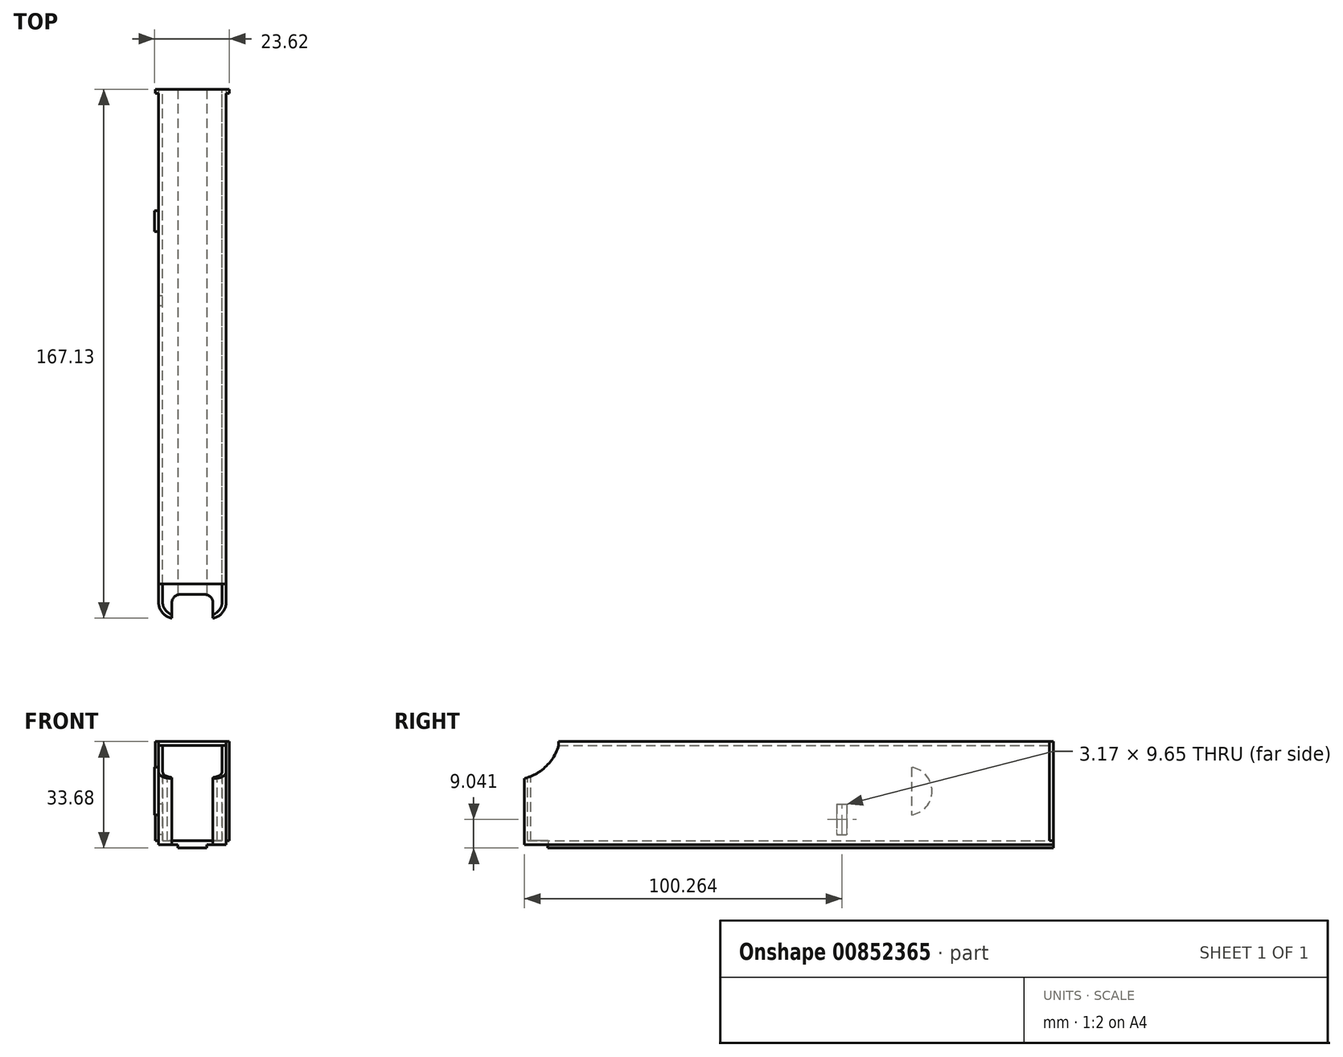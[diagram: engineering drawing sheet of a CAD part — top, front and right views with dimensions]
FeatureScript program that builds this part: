
annotation { "Feature Type Name" : "Feature", "Feature Type Description" : "" }
export const myFeature = defineFeature(function(context is Context, id is Id, definition is map)
    precondition{}
    {
        {
            var Q0;
            Q0=qCreatedBy(makeId("Front.planeOp"),FACE);
            var sketch = newSketch(context, id + "F0", { "sketchPlane" : qUnion([Q0])});
            skLineSegment(sketch, "E0.bottom", {"start": v(0, 0) * mm, "end": v(21.34, 0) * mm});
            skLineSegment(sketch, "E0.top", {"start": v(0, 32.64) * mm, "end": v(21.34, 32.64) * mm});
            skLineSegment(sketch, "E0.left", {"start": v(0, 0) * mm, "end": v(0, 32.64) * mm});
            skLineSegment(sketch, "E0.right", {"start": v(21.34, 0) * mm, "end": v(21.34, 32.64) * mm});
            skSolve(sketch);
        }
        {
            var Q0;
            Q0 = qSketchRegion(id + "F0", true);
            extrude(context, id + "F1", {"entities" : qUnion([Q0]), "depth" : 167.13 * mm, "offsetDistance" : 25.4 * mm});
        }
        {
            var Q0;
            Q0=makeQuery(id+"F1.opExtrude","CAP_FACE",FACE,{"disambiguationData":[OSD([sQuery(id+"F0.wireOp",EDGE,"E0.bottom"),sQuery(id+"F0.wireOp",EDGE,"E0.top"),sQuery(id+"F0.wireOp",EDGE,"E0.left"),sQuery(id+"F0.wireOp",EDGE,"E0.right")])],"isStart":false});
            var sketch = newSketch(context, id + "F2", { "sketchPlane" : qUnion([Q0])});
            skLineSegment(sketch, "E1.bottom", {"start": v(6.1, 0) * mm, "end": v(15.23, 0) * mm});
            skLineSegment(sketch, "E1.top", {"start": v(6.1, -1.04) * mm, "end": v(15.23, -1.04) * mm});
            skLineSegment(sketch, "E1.left", {"start": v(6.1, 0) * mm, "end": v(6.1, -1.04) * mm});
            skLineSegment(sketch, "E1.right", {"start": v(15.23, 0) * mm, "end": v(15.23, -1.04) * mm});
            skLineSegment(sketch, "E2", {"start": v(10.67, 0) * mm, "end": v(10.67, -3.56) * mm});
            skLineSegment(sketch, "E3", {"start": v(10.67, -1.04) * mm, "end": v(10.67, -2.73) * mm});
            skSolve(sketch);
        }
        {
            var Q0;
            Q0 = qSketchRegion(id + "F2", true);
            var Q1;
            Q1=makeQuery(id+"F1.opExtrude","CAP_FACE",FACE,{"disambiguationData":[OSD([sQuery(id+"F0.wireOp",EDGE,"E0.bottom"),sQuery(id+"F0.wireOp",EDGE,"E0.top"),sQuery(id+"F0.wireOp",EDGE,"E0.left"),sQuery(id+"F0.wireOp",EDGE,"E0.right")])],"isStart":true});
            extrude(context, id + "F3", {"entities" : qUnion([Q0]), "operationType" : NewBodyOperationType.ADD, "endBound" : BoundingType.UP_TO_SURFACE, "oppositeDirection" : true, "depth" : 25.4 * mm, "endBoundEntityFace" : qUnion([Q1]), "offsetDistance" : 25.4 * mm});
        }
        {
            var Q0;
            Q0=makeQuery(id+"F3.opExtrude","SWEPT_FACE",FACE,{"disambiguationData":[OSD([sQuery(id+"F2.wireOp",EDGE,"E1.top")])]});
            var sketch = newSketch(context, id + "F4", { "sketchPlane" : qUnion([Q0])});
            skLineSegment(sketch, "E4.bottom", {"start": v(4.2, 179.24) * mm, "end": v(17.14, 179.24) * mm});
            skLineSegment(sketch, "E4.top", {"start": v(6.73, 159.66) * mm, "end": v(14.6, 159.66) * mm});
            skLineSegment(sketch, "E4.left", {"start": v(4.2, 179.24) * mm, "end": v(4.2, 162.2) * mm});
            skLineSegment(sketch, "E4.right", {"start": v(17.14, 179.24) * mm, "end": v(17.14, 162.2) * mm});
            skPoint(sketch, "E5.visualSharp", {"position": v(4.2, 159.66) * mm});
            skArc(sketch, "E5.filletArc", {"start": v(4.2, 162.2) * mm, "mid": v(4.93, 160.4) * mm, "end": v(6.73, 159.66) * mm});
            skPoint(sketch, "E6.visualSharp", {"position": v(17.14, 159.66) * mm});
            skArc(sketch, "E6.filletArc", {"start": v(14.6, 159.66) * mm, "mid": v(16.4, 160.4) * mm, "end": v(17.14, 162.2) * mm});
            skLineSegment(sketch, "E7", {"start": v(10.67, 179.24) * mm, "end": v(10.67, 175.06) * mm});
            skLineSegment(sketch, "E8", {"start": v(10.67, 175.06) * mm, "end": v(10.67, 167.13) * mm});
            skSolve(sketch);
        }
        {
            var Q0;
            Q0 = qSketchRegion(id + "F4", true);
            extrude(context, id + "F5", {"entities" : qUnion([Q0]), "operationType" : NewBodyOperationType.REMOVE, "endBound" : BoundingType.THROUGH_ALL, "oppositeDirection" : true, "depth" : 25.4 * mm, "offsetDistance" : 25.4 * mm});
        }
        {
            var Q0;
            Q0=makeQuery(id+"F1.opExtrude","CAP_EDGE",EDGE,{"disambiguationData":[OSD([sQuery(id+"F0.wireOp",EDGE,"E0.left")])],"isStart":false});
            var Q1;
            Q1=makeQuery(id+"F1.opExtrude","CAP_EDGE",EDGE,{"disambiguationData":[OSD([sQuery(id+"F0.wireOp",EDGE,"E0.right")])],"isStart":false});
            fillet(context, id + "F6", {"entities" : qUnion([Q0, Q1]), "radius" : 5.08 * mm, "tangentPropagation" : true, "allowEdgeOverflow" : false});
        }
        {
            var Q0;
            Q0=makeQuery(id+"F1.opExtrude","SWEPT_FACE",FACE,{"disambiguationData":[OSD([sQuery(id+"F0.wireOp",EDGE,"E0.left")])]});
            var sketch = newSketch(context, id + "F7", { "sketchPlane" : qUnion([Q0])});
            skLineSegment(sketch, "E9", {"start": v(156.34, 32.64) * mm, "end": v(167.13, 32.64) * mm});
            skLineSegment(sketch, "E10", {"start": v(167.13, 32.64) * mm, "end": v(167.13, 20.96) * mm});
            skLineSegment(sketch, "E11", {"start": v(156.34, 32.64) * mm, "end": v(156.34, 31.37) * mm});
            skArc(sketch, "E12", {"start": v(156.34, 31.37) * mm, "mid": v(160.36, 24.74) * mm, "end": v(167.13, 20.96) * mm});
            skSolve(sketch);
        }
        {
            var Q0;
            {var subQ4=sQuery(id+"F7.wireOp",EDGE,"E11");Q0=makeQuery(id+"F7.imprint","IMPRINT",FACE,{"disambiguationData":[TD([[makeQuery(id+"F7.imprint","IMPRINT",EDGE,{"derivedFrom":subQ4}),1.0]])]});}
            var Q1;
            {var subQ4=sQuery(id+"F7.wireOp",EDGE,"E10");Q1=makeQuery(id+"F7.imprint","IMPRINT",FACE,{"disambiguationData":[TD([[makeQuery(id+"F7.imprint","IMPRINT",EDGE,{"derivedFrom":subQ4}),-1.0]])]});}
            extrude(context, id + "F8", {"entities" : qUnion([Q0, Q1]), "operationType" : NewBodyOperationType.REMOVE, "endBound" : BoundingType.THROUGH_ALL, "oppositeDirection" : true, "depth" : 25.4 * mm, "offsetDistance" : 25.4 * mm});
        }
        {
            var Q0;
            Q0=makeQuery(id+"F5.boolean.opBoolean","COPY",FACE,{"derivedFrom":makeQuery(id+"F5.opExtrude","SWEPT_FACE",FACE,{"disambiguationData":[OSD([sQuery(id+"F4.wireOp",EDGE,"E4.top")])]})});
            var Q1;
            Q1=makeQuery(id+"F8.boolean.opBoolean","COPY",FACE,{"derivedFrom":makeQuery(id+"F8.opExtrude","SWEPT_FACE",FACE,{"disambiguationData":[OSD([sQuery(id+"F7.wireOp",EDGE,"E12")])]})});
            var Q2;
            Q2=makeQuery(id+"F5.boolean.opBoolean","COPY",FACE,{"derivedFrom":makeQuery(id+"F5.opExtrude","SWEPT_FACE",FACE,{"disambiguationData":[OSD([sQuery(id+"F4.wireOp",EDGE,"E6.filletArc")])]})});
            var Q3;
            Q3=makeQuery(id+"F5.boolean.opBoolean","COPY",FACE,{"derivedFrom":makeQuery(id+"F5.opExtrude","SWEPT_FACE",FACE,{"disambiguationData":[OSD([sQuery(id+"F4.wireOp",EDGE,"E5.filletArc")])]})});
            shell(context, id + "F9", {"entities" : qUnion([Q0, Q1, Q2, Q3]), "thickness" : 1.27 * mm});
        }
        {
            var Q0;
            Q0=makeQuery(id+"F1.opExtrude","SWEPT_FACE",FACE,{"disambiguationData":[OSD([sQuery(id+"F0.wireOp",EDGE,"E0.top")])]});
            var sketch = newSketch(context, id + "F10", { "sketchPlane" : qUnion([Q0])});
            skCircle(sketch, "E13", {"center": v(15.18, -161.63) * mm, "radius": 4.89 * mm});
            skCircle(sketch, "E14", {"center": v(6.16, -161.63) * mm, "radius": 4.89 * mm});
            skSolve(sketch);
        }
        {
            var Q0;
            Q0 = qSketchRegion(id + "F10", true);
            var Q1;
            {var subQ0=sQuery(id+"F0.wireOp",EDGE,"E0.right");var subQ3=sQuery(id+"F0.wireOp",EDGE,"E0.bottom");Q1=makeQuery(id+"F9.opShell","OFFSET_FACE",FACE,{"disambiguationData":[OSD([subQ3]),TDD([makeQuery(id+"F3.boolean.opBoolean","SPLIT",FACE,{"disambiguationData":[TD([makeQuery(id+"F1.opExtrude","SWEPT_FACE",FACE,{"disambiguationData":[OSD([subQ0])]})])],"derivedFrom":makeQuery(id+"F1.opExtrude","SWEPT_FACE",FACE,{"disambiguationData":[OSD([subQ3])]})})])]});}
            extrude(context, id + "F11", {"entities" : qUnion([Q0]), "operationType" : NewBodyOperationType.REMOVE, "endBound" : BoundingType.UP_TO_SURFACE, "oppositeDirection" : true, "depth" : 25.4 * mm, "endBoundEntityFace" : qUnion([Q1]), "offsetDistance" : 25.4 * mm});
        }
        {
            var Q0;
            Q0=makeQuery(id+"F5.boolean.opBoolean","COPY",FACE,{"derivedFrom":makeQuery(id+"F5.opExtrude","SWEPT_FACE",FACE,{"disambiguationData":[OSD([sQuery(id+"F4.wireOp",EDGE,"E4.top")])]})});
            var sketch = newSketch(context, id + "F12", { "sketchPlane" : qUnion([Q0])});
            skLineSegment(sketch, "E15", {"start": v(7.31, 1.27) * mm, "end": v(13.97, 1.27) * mm});
            skLineSegment(sketch, "E16.bottom", {"start": v(7.31, 1.27) * mm, "end": v(14.07, 1.27) * mm});
            skLineSegment(sketch, "E16.top", {"start": v(7.31, 0.23) * mm, "end": v(14.07, 0.23) * mm});
            skLineSegment(sketch, "E16.left", {"start": v(7.31, 1.27) * mm, "end": v(7.31, 0.23) * mm});
            skLineSegment(sketch, "E16.right", {"start": v(14.07, 1.27) * mm, "end": v(14.07, 0.23) * mm});
            skSolve(sketch);
        }
        {
            var Q0;
            Q0 = qSketchRegion(id + "F12", true);
            var Q1;
            Q1=makeQuery(id+"F9.opShell","OFFSET_FACE",FACE,{"disambiguationData":[OSD([sQuery(id+"F0.wireOp",EDGE,"E0.bottom"),sQuery(id+"F0.wireOp",EDGE,"E0.top"),sQuery(id+"F0.wireOp",EDGE,"E0.left"),sQuery(id+"F0.wireOp",EDGE,"E0.right")])]});
            extrude(context, id + "F13", {"entities" : qUnion([Q0]), "operationType" : NewBodyOperationType.ADD, "endBound" : BoundingType.UP_TO_SURFACE, "oppositeDirection" : true, "depth" : 25.4 * mm, "endBoundEntityFace" : qUnion([Q1]), "offsetDistance" : 25.4 * mm});
        }
        {
            var Q0;
            {var subQ0=sQuery(id+"F0.wireOp",EDGE,"E0.right");var subQ1=sQuery(id+"F0.wireOp",EDGE,"E0.left");var subQ2=sQuery(id+"F0.wireOp",EDGE,"E0.top");var subQ3=sQuery(id+"F0.wireOp",EDGE,"E0.bottom");Q0=makeQuery(id+"F3.boolean.opBoolean","MERGE",FACE,{"derivedFrom":[makeQuery(id+"F1.opExtrude","CAP_FACE",FACE,{"disambiguationData":[OSD([subQ3,subQ2,subQ1,subQ0])],"isStart":true}),makeQuery(id+"F3.opExtrude","CAP_FACE",FACE,{"disambiguationData":[OSD([subQ3,subQ2,subQ1,subQ0])],"isStart":false})]});}
            var sketch = newSketch(context, id + "F14", { "sketchPlane" : qUnion([Q0])});
            skLineSegment(sketch, "E17.bottom", {"start": v(-20.07, 31.37) * mm, "end": v(-1.27, 31.37) * mm});
            skLineSegment(sketch, "E17.top", {"start": v(-20.07, 1.27) * mm, "end": v(-1.27, 1.27) * mm});
            skLineSegment(sketch, "E17.left", {"start": v(-20.07, 31.37) * mm, "end": v(-20.07, 1.27) * mm});
            skLineSegment(sketch, "E17.right", {"start": v(-1.27, 31.37) * mm, "end": v(-1.27, 1.27) * mm});
            skSolve(sketch);
        }
        {
            var Q0;
            Q0 = qSketchRegion(id + "F14", true);
            extrude(context, id + "F15", {"entities" : qUnion([Q0]), "operationType" : NewBodyOperationType.REMOVE, "oppositeDirection" : true, "depth" : 25.4 * mm, "offsetDistance" : 25.4 * mm});
        }
        {
            var Q0;
            Q0=makeQuery(id+"F1.opExtrude","SWEPT_FACE",FACE,{"disambiguationData":[OSD([sQuery(id+"F0.wireOp",EDGE,"E0.top")])]});
            var sketch = newSketch(context, id + "F16", { "sketchPlane" : qUnion([Q0])});
            skLineSegment(sketch, "E18", {"start": v(0, 0) * mm, "end": v(-1.02, 0) * mm});
            skLineSegment(sketch, "E19", {"start": v(-1.02, 0) * mm, "end": v(-1.02, -1.27) * mm});
            skLineSegment(sketch, "E20", {"start": v(-1.02, -1.27) * mm, "end": v(0, -1.27) * mm});
            skLineSegment(sketch, "E21.bottom", {"start": v(21.34, 0) * mm, "end": v(22.35, 0) * mm});
            skLineSegment(sketch, "E21.top", {"start": v(21.34, -1.27) * mm, "end": v(22.35, -1.27) * mm});
            skLineSegment(sketch, "E21.left", {"start": v(21.34, 0) * mm, "end": v(21.34, -1.27) * mm});
            skLineSegment(sketch, "E21.right", {"start": v(22.35, 0) * mm, "end": v(22.35, -1.27) * mm});
            skSolve(sketch);
        }
        {
            var Q0;
            Q0 = qSketchRegion(id + "F16", true);
            var Q1;
            {var subQ0=sQuery(id+"F16.wireOp",EDGE,"E18");Q1=makeQuery(id+"F16.imprint","IMPRINT",FACE,{"disambiguationData":[TD([[makeQuery(id+"F16.imprint","IMPRINT",EDGE,{"derivedFrom":subQ0}),1.0]])]});}
            var Q2;
            {var subQ0=makeQuery(id+"F11.opExtrude","CAP_FACE",FACE,{"disambiguationData":[OSD([sQuery(id+"F10.wireOp",EDGE,"E13"),sQuery(id+"F10.wireOp",EDGE,"E14")])],"isStart":false});var subQ1=sQuery(id+"F0.wireOp",EDGE,"E0.right");var subQ2=sQuery(id+"F0.wireOp",EDGE,"E0.left");var subQ4=sQuery(id+"F0.wireOp",EDGE,"E0.bottom");var subQ11=makeQuery(id+"F1.opExtrude","SWEPT_FACE",FACE,{"disambiguationData":[OSD([subQ4])]});Q2=makeQuery(id+"F15.boolean.opBoolean","MERGE",FACE,{"derivedFrom":[makeQuery(id+"F13.boolean.opBoolean","MERGE",FACE,{"derivedFrom":[makeQuery(id+"F11.boolean.opBoolean","MERGE",FACE,{"derivedFrom":[makeQuery(id+"F9.opShell","OFFSET_FACE",FACE,{"disambiguationData":[OSD([subQ4]),TDD([makeQuery(id+"F3.boolean.opBoolean","SPLIT",FACE,{"disambiguationData":[TD([makeQuery(id+"F1.opExtrude","SWEPT_FACE",FACE,{"disambiguationData":[OSD([subQ2])]})])],"derivedFrom":subQ11})])]}),subQ0]}),makeQuery(id+"F11.boolean.opBoolean","MERGE",FACE,{"derivedFrom":[makeQuery(id+"F9.opShell","OFFSET_FACE",FACE,{"disambiguationData":[OSD([subQ4]),TDD([makeQuery(id+"F3.boolean.opBoolean","SPLIT",FACE,{"disambiguationData":[TD([makeQuery(id+"F1.opExtrude","SWEPT_FACE",FACE,{"disambiguationData":[OSD([subQ1])]})])],"derivedFrom":subQ11})])]}),subQ0]}),makeQuery(id+"F13.opExtrude","SWEPT_FACE",FACE,{"disambiguationData":[OSD([sQuery(id+"F12.wireOp",EDGE,"E16.bottom")])]})]}),makeQuery(id+"F15.opExtrude","SWEPT_FACE",FACE,{"disambiguationData":[OSD([sQuery(id+"F14.wireOp",EDGE,"E17.top")])]})]});}
            extrude(context, id + "F17", {"entities" : qUnion([Q0, Q1]), "operationType" : NewBodyOperationType.ADD, "endBound" : BoundingType.UP_TO_SURFACE, "oppositeDirection" : true, "depth" : 25.4 * mm, "endBoundEntityFace" : qUnion([Q2]), "offsetDistance" : 25.4 * mm});
        }
        {
            var Q0;
            Q0=makeQuery(id+"F1.opExtrude","SWEPT_FACE",FACE,{"disambiguationData":[OSD([sQuery(id+"F0.wireOp",EDGE,"E0.left")])]});
            var sketch = newSketch(context, id + "F18", { "sketchPlane" : qUnion([Q0])});
            skLineSegment(sketch, "E22", {"start": v(44.9, 24.5) * mm, "end": v(44.9, 9.42) * mm});
            skArc(sketch, "E23", {"start": v(44.9, 24.5) * mm, "mid": v(38.4, 16.95) * mm, "end": v(44.9, 9.42) * mm});
            skSolve(sketch);
        }
        {
            var Q0;
            Q0 = qSketchRegion(id + "F18", true);
            extrude(context, id + "F19", {"entities" : qUnion([Q0]), "operationType" : NewBodyOperationType.ADD, "depth" : 1.27 * mm, "offsetDistance" : 25.4 * mm});
        }
        {
            var Q0;
            Q0=makeQuery(id+"F1.opExtrude","SWEPT_FACE",FACE,{"disambiguationData":[OSD([sQuery(id+"F0.wireOp",EDGE,"E0.left")])]});
            var sketch = newSketch(context, id + "F20", { "sketchPlane" : qUnion([Q0])});
            skLineSegment(sketch, "E24.bottom", {"start": v(68.45, 12.83) * mm, "end": v(65.28, 12.83) * mm});
            skLineSegment(sketch, "E24.top", {"start": v(68.45, 3.18) * mm, "end": v(65.28, 3.17) * mm});
            skLineSegment(sketch, "E24.left", {"start": v(68.45, 12.83) * mm, "end": v(68.45, 3.18) * mm});
            skLineSegment(sketch, "E24.right", {"start": v(65.28, 12.83) * mm, "end": v(65.28, 3.18) * mm});
            skSolve(sketch);
        }
        {
            var Q0;
            Q0 = qSketchRegion(id + "F20", true);
            extrude(context, id + "F21", {"entities" : qUnion([Q0]), "operationType" : NewBodyOperationType.REMOVE, "oppositeDirection" : true, "depth" : 12.7 * mm, "offsetDistance" : 25.4 * mm});
        }
    });
